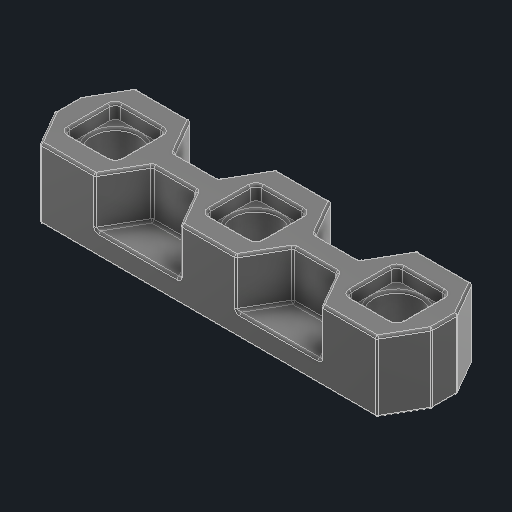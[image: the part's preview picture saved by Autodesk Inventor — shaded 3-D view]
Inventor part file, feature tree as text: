
AUTODESK INVENTOR PART (.ipt)
format: ipt  version: 2025 (Build 290162000, 162)  size: 510,464 bytes
history: native  units: in
note: dims shown in document units (in); Inventor stores cm internally (conversion verified against a paired STEP export)
features: other x3, sketch x1
ambient origin geometry x8: Origin, YZ Plane, XZ Plane, XY Plane, X Axis, Y Axis, Z Axis, Center Point
bodies: Solid1 (feature_tree)
feature tree (4):
  other  "Bearing Flat Low Profile.ipt"
  other  "Solid1::Bearing Flat Low Profile.ipt"
  other  "TaggingFeature1"
  sketch  "Sketch1"  dims[d0=0.3937in]
